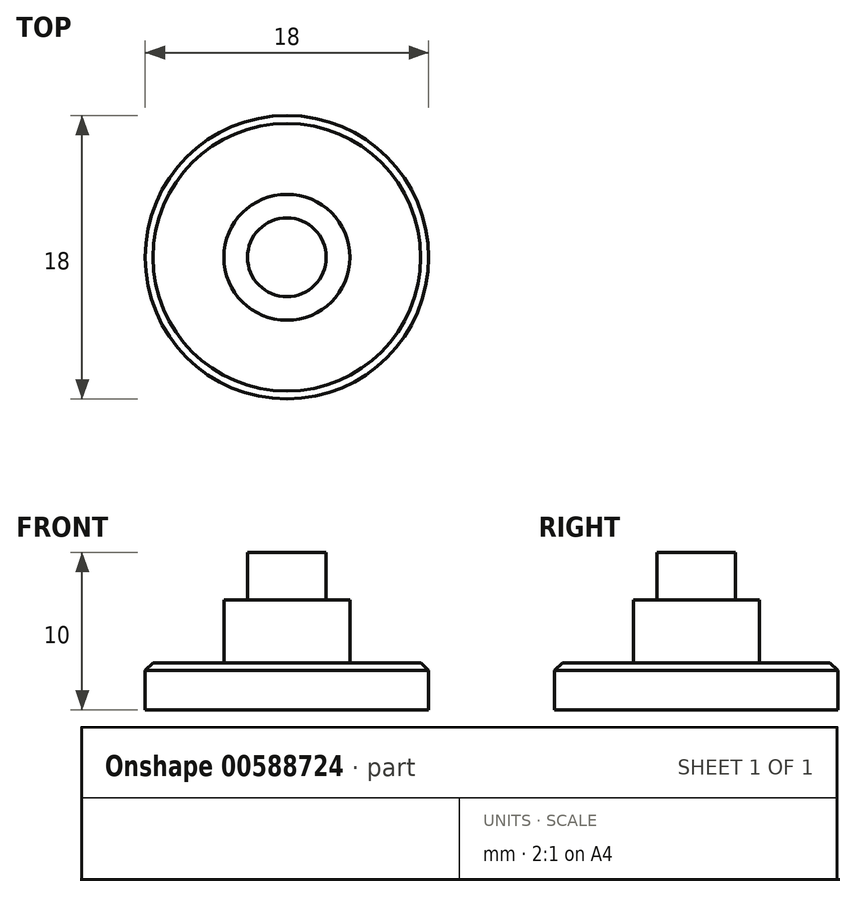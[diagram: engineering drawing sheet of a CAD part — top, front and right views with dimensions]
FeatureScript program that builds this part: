
annotation { "Feature Type Name" : "Feature", "Feature Type Description" : "" }
export const myFeature = defineFeature(function(context is Context, id is Id, definition is map)
    precondition{}
    {
        {
            var Q0;
            Q0=qCreatedBy(makeId("Top.planeOp"),FACE);
            var sketch = newSketch(context, id + "F0", { "sketchPlane" : qUnion([Q0])});
            skCircle(sketch, "E0", {"center": v(0, 0) * mm, "radius": 9 * mm});
            skSolve(sketch);
        }
        {
            var Q0;
            Q0=makeQuery(id+"F0.imprint","IMPRINT",FACE,{"disambiguationData":[TD([[makeQuery(id+"F0.imprint","IMPRINT",EDGE,{"derivedFrom":sQuery(id+"F0.wireOp",EDGE,"E0")}),1.0]])]});
            extrude(context, id + "F1", {"entities" : qUnion([Q0]), "depth" : 3 * mm, "offsetDistance" : 25 * mm});
        }
        {
            var Q0;
            Q0=makeQuery(id+"F1.opExtrude","CAP_EDGE",EDGE,{"disambiguationData":[OSD([sQuery(id+"F0.wireOp",EDGE,"E0")])],"isStart":false});
            chamfer(context, id + "F2", {"entities" : qUnion([Q0]), "width" : .5 * mm, "tangentPropagation" : true});
        }
        {
            var Q0;
            Q0=makeQuery(id+"F1.opExtrude","CAP_FACE",FACE,{"disambiguationData":[OSD([sQuery(id+"F0.wireOp",EDGE,"E0")])],"isStart":false});
            var sketch = newSketch(context, id + "F3", { "sketchPlane" : qUnion([Q0])});
            skCircle(sketch, "E1", {"center": v(0, 0) * mm, "radius": 4 * mm});
            skSolve(sketch);
        }
        {
            var Q0;
            Q0 = qSketchRegion(id + "F3", true);
            extrude(context, id + "F4", {"entities" : qUnion([Q0]), "operationType" : NewBodyOperationType.ADD, "depth" : 4 * mm, "offsetDistance" : 25 * mm});
        }
        {
            var Q0;
            Q0=makeQuery(id+"F4.opExtrude","CAP_FACE",FACE,{"disambiguationData":[OSD([sQuery(id+"F3.wireOp",EDGE,"E1")])],"isStart":false});
            var sketch = newSketch(context, id + "F5", { "sketchPlane" : qUnion([Q0])});
            skCircle(sketch, "E2", {"center": v(0, 0) * mm, "radius": 2.5 * mm});
            skSolve(sketch);
        }
        {
            var Q0;
            Q0 = qSketchRegion(id + "F5", true);
            extrude(context, id + "F6", {"entities" : qUnion([Q0]), "operationType" : NewBodyOperationType.ADD, "depth" : 3 * mm, "offsetDistance" : 25 * mm});
        }
    });
